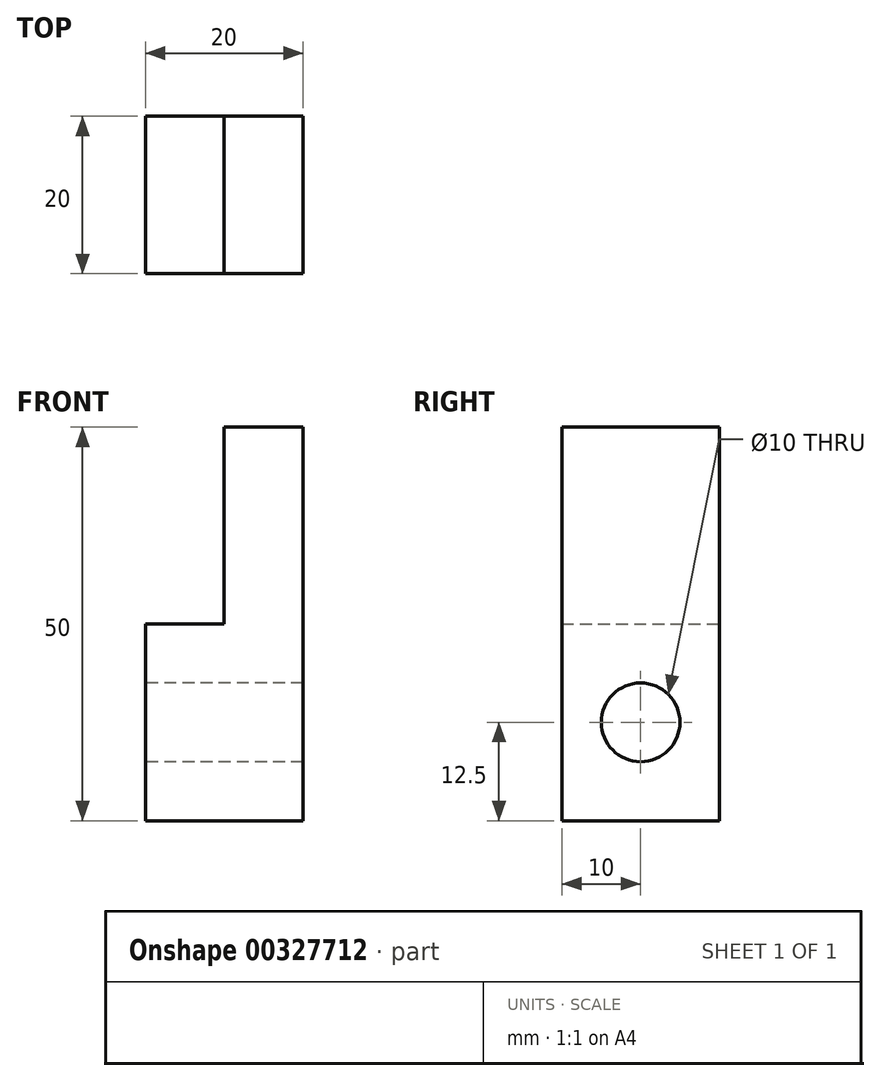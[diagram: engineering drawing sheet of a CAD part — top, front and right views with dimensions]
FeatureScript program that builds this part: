
annotation { "Feature Type Name" : "Feature", "Feature Type Description" : "" }
export const myFeature = defineFeature(function(context is Context, id is Id, definition is map)
    precondition{}
    {
        {
            var Q0;
            Q0=qCreatedBy(makeId("Top.planeOp"),FACE);
            var sketch = newSketch(context, id + "F0", { "sketchPlane" : qUnion([Q0])});
            skLineSegment(sketch, "E0.bottom", {"start": v(10, -10) * mm, "end": v(-10, -10) * mm});
            skLineSegment(sketch, "E0.top", {"start": v(10, 10) * mm, "end": v(-10, 10) * mm});
            skLineSegment(sketch, "E0.left", {"start": v(10, -10) * mm, "end": v(10, 10) * mm});
            skLineSegment(sketch, "E0.right", {"start": v(-10, -10) * mm, "end": v(-10, 10) * mm});
            skPoint(sketch, "E0.middle", {"position": v(0, 0) * mm});
            skSolve(sketch);
        }
        {
            var Q0;
            Q0=makeQuery(id+"F0.imprint","IMPRINT",FACE,{"disambiguationData":[TD([[makeQuery(id+"F0.imprint","IMPRINT",EDGE,{"derivedFrom":sQuery(id+"F0.wireOp",EDGE,"E0.bottom")}),-1.0]])]});
            extrude(context, id + "F1", {"entities" : qUnion([Q0]), "depth" : 50 * mm});
        }
        {
            var Q0;
            Q0=makeQuery(id+"F1.opExtrude","CAP_FACE",FACE,{"disambiguationData":[OSD([sQuery(id+"F0.wireOp",EDGE,"E0.bottom"),sQuery(id+"F0.wireOp",EDGE,"E0.top"),sQuery(id+"F0.wireOp",EDGE,"E0.left"),sQuery(id+"F0.wireOp",EDGE,"E0.right")])],"isStart":false});
            var sketch = newSketch(context, id + "F2", { "sketchPlane" : qUnion([Q0])});
            skLineSegment(sketch, "E1.bottom", {"start": v(0, -10) * mm, "end": v(-10, -10) * mm});
            skLineSegment(sketch, "E1.top", {"start": v(0, 10) * mm, "end": v(-10, 10) * mm});
            skLineSegment(sketch, "E1.left", {"start": v(0, -10) * mm, "end": v(0, 10) * mm});
            skLineSegment(sketch, "E1.right", {"start": v(-10, -10) * mm, "end": v(-10, 10) * mm});
            skSolve(sketch);
        }
        {
            var Q0;
            Q0=makeQuery(id+"F2.imprint","IMPRINT",FACE,{"disambiguationData":[TD([[makeQuery(id+"F2.imprint","IMPRINT",EDGE,{"derivedFrom":sQuery(id+"F2.wireOp",EDGE,"E1.bottom")}),-1.0]])]});
            extrude(context, id + "F3", {"entities" : qUnion([Q0]), "operationType" : NewBodyOperationType.REMOVE, "oppositeDirection" : true, "depth" : 25 * mm});
        }
        {
            var Q0;
            Q0=makeQuery(id+"F1.opExtrude","SWEPT_FACE",FACE,{"disambiguationData":[OSD([sQuery(id+"F0.wireOp",EDGE,"E0.right")])]});
            var sketch = newSketch(context, id + "F4", { "sketchPlane" : qUnion([Q0])});
            skCircle(sketch, "E2", {"center": v(0, 12.5) * mm, "radius": 5 * mm});
            skSolve(sketch);
        }
        {
            var Q0;
            Q0=makeQuery(id+"F4.imprint","IMPRINT",FACE,{"disambiguationData":[TD([[makeQuery(id+"F4.imprint","IMPRINT",EDGE,{"derivedFrom":sQuery(id+"F4.wireOp",EDGE,"E2")}),1.0]])]});
            extrude(context, id + "F5", {"entities" : qUnion([Q0]), "operationType" : NewBodyOperationType.REMOVE, "oppositeDirection" : true, "depth" : 50 * mm});
        }
    });
